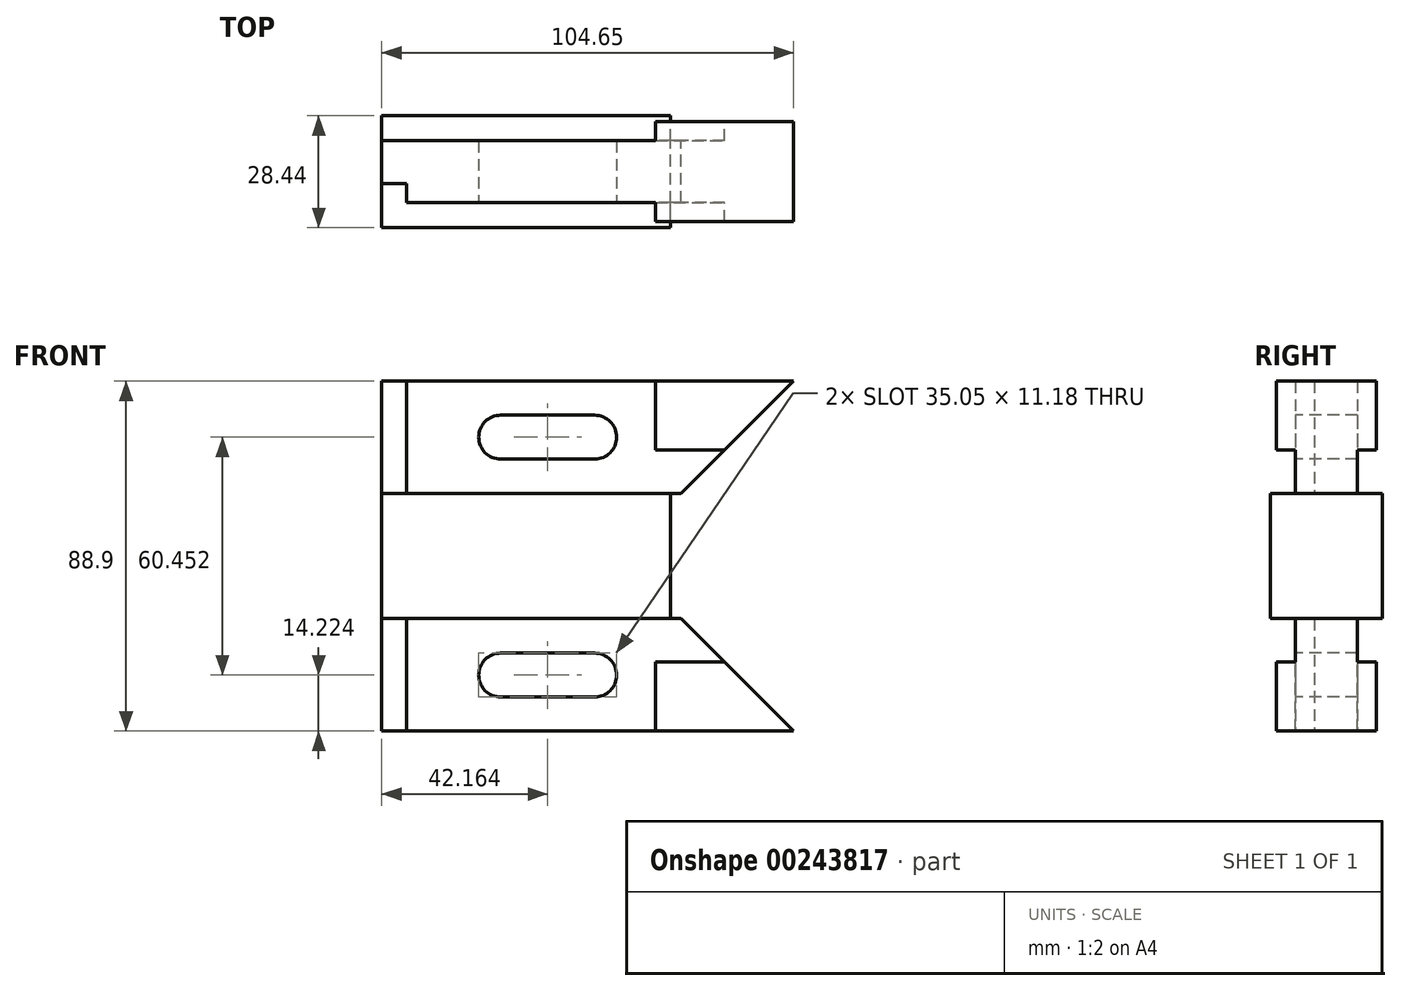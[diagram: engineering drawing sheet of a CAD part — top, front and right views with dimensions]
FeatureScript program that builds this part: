
annotation { "Feature Type Name" : "Feature", "Feature Type Description" : "" }
export const myFeature = defineFeature(function(context is Context, id is Id, definition is map)
    precondition{}
    {
        {
            var Q0;
            Q0=qCreatedBy(makeId("Front.planeOp"),FACE);
            var sketch = newSketch(context, id + "F0", { "sketchPlane" : qUnion([Q0])});
            skSolve(sketch);
        }
        {
            var Q0;
            Q0=qCreatedBy(makeId("Front.planeOp"),FACE);
            var sketch = newSketch(context, id + "F1", { "sketchPlane" : qUnion([Q0])});
            skSolve(sketch);
        }
        {
            var Q0;
            Q0=qCreatedBy(makeId("Front.planeOp"),FACE);
            var sketch = newSketch(context, id + "F2", { "sketchPlane" : qUnion([Q0])});
            skLineSegment(sketch, "E0", {"start": v(0, 44.45) * mm, "end": v(0, -44.45) * mm});
            skLineSegment(sketch, "E1", {"start": v(0, 44.45) * mm, "end": v(104.65, 44.45) * mm});
            skLineSegment(sketch, "E2", {"start": v(104.65, 44.45) * mm, "end": v(76.07, 15.87) * mm});
            skLineSegment(sketch, "E3", {"start": v(76.07, 15.87) * mm, "end": v(0, 15.87) * mm});
            skLineSegment(sketch, "E4", {"start": v(0, -44.45) * mm, "end": v(104.65, -44.45) * mm});
            skLineSegment(sketch, "E5", {"start": v(104.65, -44.45) * mm, "end": v(76.07, -15.88) * mm});
            skLineSegment(sketch, "E6", {"start": v(76.07, -15.88) * mm, "end": v(0, -15.88) * mm});
            skLineSegment(sketch, "E7", {"start": v(73.4, 15.87) * mm, "end": v(73.4, -15.88) * mm});
            skLineSegment(sketch, "E8", {"start": v(6.35, 44.45) * mm, "end": v(6.35, 15.87) * mm});
            skLineSegment(sketch, "E9", {"start": v(6.35, -15.88) * mm, "end": v(6.35, -44.45) * mm});
            skLineSegment(sketch, "E10", {"start": v(69.6, 26.92) * mm, "end": v(87.12, 26.92) * mm});
            skLineSegment(sketch, "E11", {"start": v(69.6, -44.45) * mm, "end": v(69.6, -26.92) * mm});
            skLineSegment(sketch, "E12", {"start": v(69.6, -26.92) * mm, "end": v(87.12, -26.92) * mm});
            skPoint(sketch, "E13.start.orphan", {"position": v(69.6, 44.45) * mm});
            skLineSegment(sketch, "E14", {"start": v(69.6, 44.45) * mm, "end": v(69.6, 26.92) * mm});
            skSolve(sketch);
        }
        {
            var Q0;
            {var subQ4=sQuery(id+"F2.wireOp",EDGE,"E7");Q0=makeQuery(id+"F2.imprint","IMPRINT",FACE,{"disambiguationData":[TD([[makeQuery(id+"F2.imprint","IMPRINT",EDGE,{"derivedFrom":subQ4}),-1.0]])]});}
            extrude(context, id + "F3", {"entities" : qUnion([Q0]), "endBound" : BoundingType.SYMMETRIC, "depth" : 28.45 * mm});
        }
        {
            var Q0;
            Q0=qSketchRegion(id+"F0",true);
            var Q1;
            Q1=qSketchRegion(id+"F1",true);
            var Q2;
            {var subQ4=sQuery(id+"F2.wireOp",EDGE,"E8");Q2=makeQuery(id+"F2.imprint","IMPRINT",FACE,{"disambiguationData":[TD([[makeQuery(id+"F2.imprint","IMPRINT",EDGE,{"derivedFrom":subQ4}),1.0]])]});}
            var Q3;
            {var subQ5=sQuery(id+"F2.wireOp",EDGE,"E8");Q3=makeQuery(id+"F2.imprint","IMPRINT",FACE,{"disambiguationData":[TD([[makeQuery(id+"F2.imprint","IMPRINT",EDGE,{"derivedFrom":subQ5}),-1.0]])]});}
            var Q4;
            {var subQ5=sQuery(id+"F2.wireOp",EDGE,"E9");Q4=makeQuery(id+"F2.imprint","IMPRINT",FACE,{"disambiguationData":[TD([[makeQuery(id+"F2.imprint","IMPRINT",EDGE,{"derivedFrom":subQ5}),-1.0]])]});}
            var Q5;
            {var subQ2=sQuery(id+"F2.wireOp",EDGE,"E9");Q5=makeQuery(id+"F2.imprint","IMPRINT",FACE,{"disambiguationData":[TD([[makeQuery(id+"F2.imprint","IMPRINT",EDGE,{"derivedFrom":subQ2}),1.0]])]});}
            extrude(context, id + "F4", {"entities" : qUnion([Q0, Q1, Q2, Q3, Q4, Q5]), "operationType" : NewBodyOperationType.ADD, "endBound" : BoundingType.SYMMETRIC, "depth" : 15.75 * mm});
        }
        {
            var Q0;
            {var subQ4=sQuery(id+"F2.wireOp",EDGE,"E10");Q0=makeQuery(id+"F2.imprint","IMPRINT",FACE,{"disambiguationData":[TD([[makeQuery(id+"F2.imprint","IMPRINT",EDGE,{"derivedFrom":subQ4}),1.0]])]});}
            var Q1;
            {var subQ3=sQuery(id+"F2.wireOp",EDGE,"E11");Q1=makeQuery(id+"F2.imprint","IMPRINT",FACE,{"disambiguationData":[TD([[makeQuery(id+"F2.imprint","IMPRINT",EDGE,{"derivedFrom":subQ3}),-1.0]])]});}
            extrude(context, id + "F5", {"entities" : qUnion([Q0, Q1]), "operationType" : NewBodyOperationType.ADD, "endBound" : BoundingType.SYMMETRIC, "depth" : 25.4 * mm});
        }
        {
            var Q0;
            Q0=makeQuery(id+"F4.opExtrude","CAP_FACE",FACE,{"disambiguationData":[OSD([sQuery(id+"F2.wireOp",EDGE,"E0"),sQuery(id+"F2.wireOp",EDGE,"E1"),sQuery(id+"F2.wireOp",EDGE,"E2"),sQuery(id+"F2.wireOp",EDGE,"E3"),sQuery(id+"F2.wireOp",EDGE,"E10"),sQuery(id+"F2.wireOp",EDGE,"E14")])],"isStart":false});
            var sketch = newSketch(context, id + "F6", { "sketchPlane" : qUnion([Q0])});
            skLineSegment(sketch, "E15.0", {"start": v(6.35, 44.45) * mm, "end": v(6.35, 15.87) * mm});
            skLineSegment(sketch, "E16.0", {"start": v(0, 44.45) * mm, "end": v(6.35, 44.45) * mm});
            skLineSegment(sketch, "E17.0", {"start": v(0, 44.45) * mm, "end": v(0, -44.45) * mm});
            skLineSegment(sketch, "E18.0", {"start": v(6.35, 15.87) * mm, "end": v(0, 15.87) * mm});
            skLineSegment(sketch, "E19.0", {"start": v(6.35, -15.88) * mm, "end": v(6.35, -44.45) * mm});
            skLineSegment(sketch, "E20.0", {"start": v(0, -44.45) * mm, "end": v(6.35, -44.45) * mm});
            skLineSegment(sketch, "E21.0", {"start": v(6.35, -15.88) * mm, "end": v(0, -15.88) * mm});
            skPoint(sketch, "E22.orphan", {"position": v(104.65, 44.45) * mm});
            skPoint(sketch, "E23.orphan", {"position": v(76.07, 15.87) * mm});
            skPoint(sketch, "E24.orphan", {"position": v(76.07, -15.88) * mm});
            skPoint(sketch, "E25.orphan", {"position": v(104.65, -44.45) * mm});
            skSolve(sketch);
        }
        {
            var Q0;
            Q0=makeQuery(id+"F6.imprint","IMPRINT",FACE,{"disambiguationData":[TD([[makeQuery(id+"F6.imprint","IMPRINT",EDGE,{"derivedFrom":sQuery(id+"F6.wireOp",EDGE,"E15.0")}),-1.0]])]});
            var Q1;
            Q1=makeQuery(id+"F6.imprint","IMPRINT",FACE,{"disambiguationData":[TD([[makeQuery(id+"F6.imprint","IMPRINT",EDGE,{"derivedFrom":sQuery(id+"F6.wireOp",EDGE,"E19.0")}),-1.0]])]});
            extrude(context, id + "F7", {"entities" : qUnion([Q0, Q1]), "operationType" : NewBodyOperationType.REMOVE, "oppositeDirection" : true, "depth" : 4.83 * mm});
        }
        {
            var Q0;
            Q0=makeQuery(id+"F4.opExtrude","CAP_FACE",FACE,{"disambiguationData":[OSD([sQuery(id+"F2.wireOp",EDGE,"E0"),sQuery(id+"F2.wireOp",EDGE,"E4"),sQuery(id+"F2.wireOp",EDGE,"E5"),sQuery(id+"F2.wireOp",EDGE,"E6"),sQuery(id+"F2.wireOp",EDGE,"E11"),sQuery(id+"F2.wireOp",EDGE,"E12")])],"isStart":false});
            var sketch = newSketch(context, id + "F8", { "sketchPlane" : qUnion([Q0])});
            skLineSegment(sketch, "E26", {"start": v(30.23, -30.23) * mm, "end": v(54.1, -30.23) * mm, "construction": true});
            skLineSegment(sketch, "E27", {"start": v(30.23, 30.23) * mm, "end": v(54.1, 30.23) * mm, "construction": true});
            skArc(sketch, "E28.0.startCap", {"start": v(30.23, 24.64) * mm, "mid": v(24.64, 30.23) * mm, "end": v(30.23, 35.81) * mm});
            skArc(sketch, "E28.0.endCap", {"start": v(54.1, 35.81) * mm, "mid": v(59.69, 30.23) * mm, "end": v(54.1, 24.64) * mm});
            skLineSegment(sketch, "E28.0.left", {"start": v(30.23, 35.81) * mm, "end": v(54.1, 35.81) * mm});
            skLineSegment(sketch, "E28.0.right", {"start": v(30.23, 24.64) * mm, "end": v(54.1, 24.64) * mm});
            skArc(sketch, "E29.0.startCap", {"start": v(30.23, -35.81) * mm, "mid": v(24.64, -30.23) * mm, "end": v(30.23, -24.64) * mm});
            skArc(sketch, "E29.0.endCap", {"start": v(54.1, -24.64) * mm, "mid": v(59.69, -30.23) * mm, "end": v(54.1, -35.81) * mm});
            skLineSegment(sketch, "E29.0.left", {"start": v(30.23, -24.64) * mm, "end": v(54.1, -24.64) * mm});
            skLineSegment(sketch, "E29.0.right", {"start": v(30.23, -35.81) * mm, "end": v(54.1, -35.81) * mm});
            skSolve(sketch);
        }
        {
            var Q0;
            Q0=qSketchRegion(id+"F8",true);
            extrude(context, id + "F9", {"entities" : qUnion([Q0]), "operationType" : NewBodyOperationType.REMOVE, "oppositeDirection" : true, "depth" : 25.4 * mm});
        }
    });
